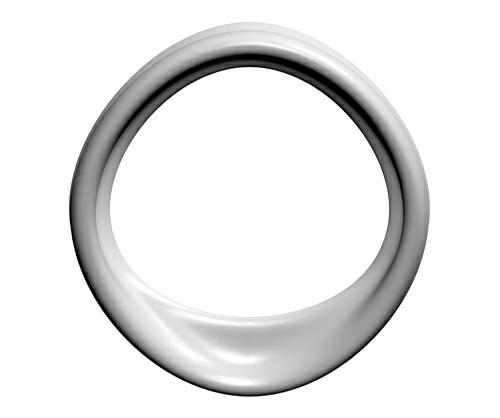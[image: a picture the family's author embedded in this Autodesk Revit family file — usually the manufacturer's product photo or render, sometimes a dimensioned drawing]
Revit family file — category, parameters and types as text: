
# Revit family: CITY ALPHABET litera „O” pionowo
name_source: partatom
category: Meble
revit_build: Autodesk Revit 2018 (Build: 20190510_1515(x64)
units: mm (PartAtom-declared; Revit-internal decimal feet)

## family parameters
Numer OmniClass = 23.40.10.11.14
Obiekt nadrzędny = Powierzchnia
Punkt obliczania pomieszczeń = Nie
Tnij formami wycięć po wczytaniu = Nie
Tytuł OmniClass = Exterior Seating
Współdzielony = Nie

## types (1)
- CITY ALPHABET litera „O"
    Domyślna rzędna = 1219 mm
    Długość = 720 mm  [stored 2.3622 ft]
    IfcExportAs = IfcFurnishingElement
    Komentarze do typu = Ławka
    Materiał - informacja = Szeroki wybór kolorów wg palety RAL. Istnieje również możliwość specjalnego wykonania
kolorystycznego na indywidualne zapytanie klienta.
    Model = CITY ALPHABET litera „O”
    Obraz typu = O.jpg
    Producent = Astrini Design
    Szerokość = 1850 mm  [stored 6.06955 ft]
    Temepratura użytkowania = -40°C do 80°C, ( -40°F do 176°F )
    URL = http://astrini-design.pl
    Waga (szacunkowo) = 60.00 kg
    Waga po wypełnieniu (szacunkowo) = 110.00 kg
    Wysokość = 1900 mm  [stored 6.2336 ft]

note: [stored X ft] marks values corroborated as IEEE doubles in the binary element streams (Revit-internal decimal feet)
